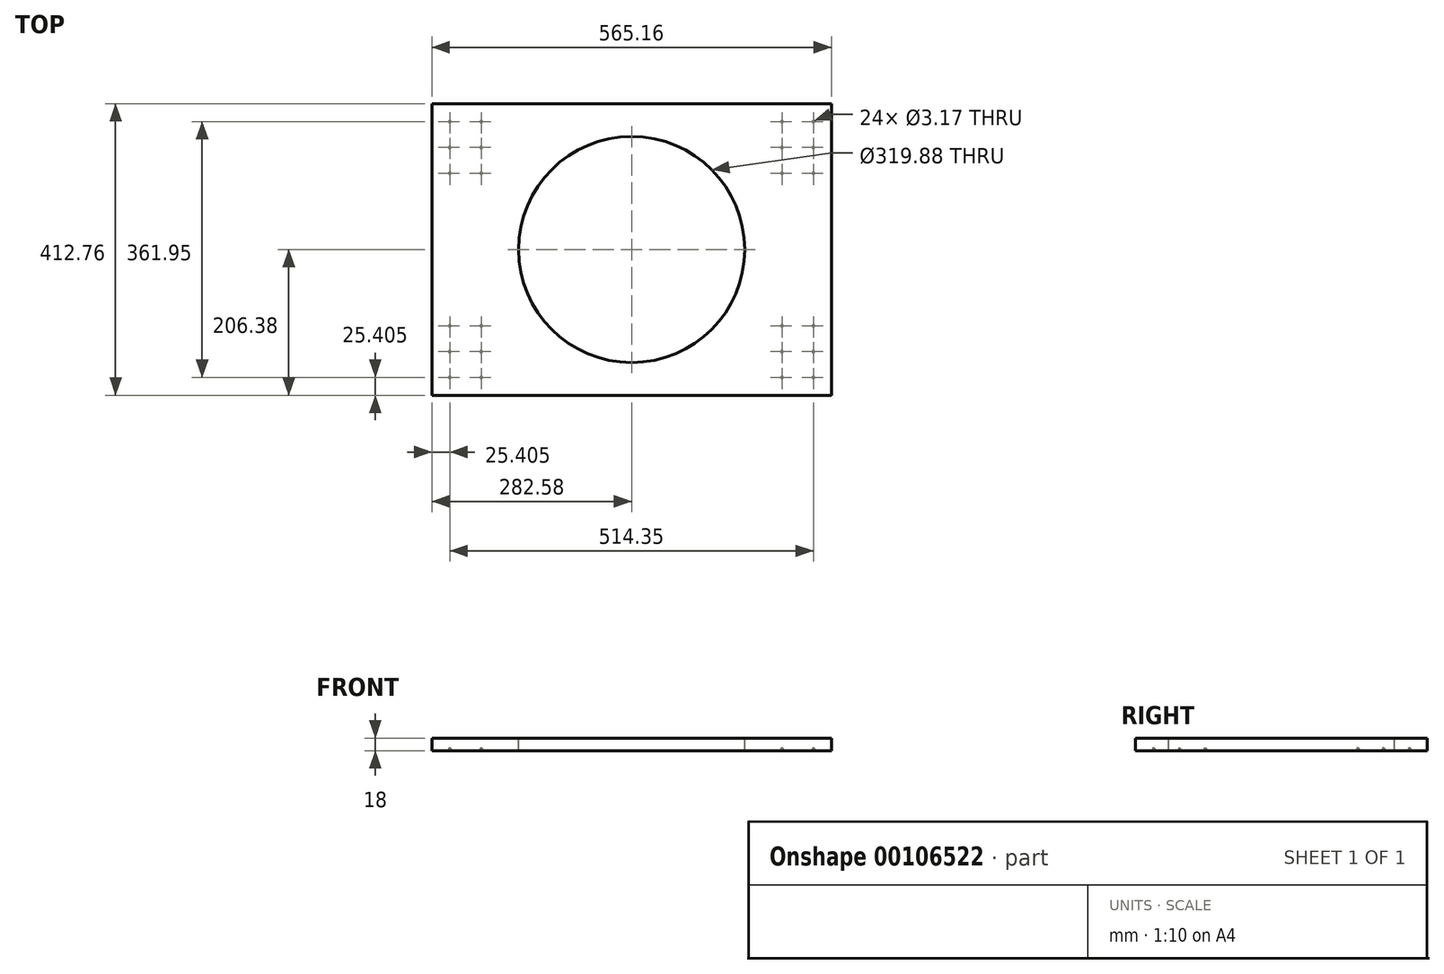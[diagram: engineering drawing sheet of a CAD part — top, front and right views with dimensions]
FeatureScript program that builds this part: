
annotation { "Feature Type Name" : "Feature", "Feature Type Description" : "" }
export const myFeature = defineFeature(function(context is Context, id is Id, definition is map)
    precondition{}
    {
        {
            var Q0;
            Q0=qCreatedBy(makeId("Top.planeOp"),FACE);
            var sketch = newSketch(context, id + "F0", { "sketchPlane" : qUnion([Q0])});
            skLineSegment(sketch, "E0.bottom", {"start": v(282.58, -206.38) * mm, "end": v(-282.57, -206.38) * mm});
            skLineSegment(sketch, "E0.top", {"start": v(282.57, 206.38) * mm, "end": v(-282.57, 206.38) * mm});
            skLineSegment(sketch, "E0.left", {"start": v(282.57, -206.38) * mm, "end": v(282.57, 206.38) * mm});
            skLineSegment(sketch, "E0.right", {"start": v(-282.57, -206.38) * mm, "end": v(-282.57, 206.37) * mm});
            skPoint(sketch, "E0.middle", {"position": v(0, 0) * mm});
            skSolve(sketch);
        }
        {
            var Q0;
            Q0=makeQuery(id+"F0.imprint","IMPRINT",FACE,{"disambiguationData":[TD([[makeQuery(id+"F0.imprint","IMPRINT",EDGE,{"derivedFrom":sQuery(id+"F0.wireOp",EDGE,"E0.bottom")}),-1.0]])]});
            extrude(context, id + "F1", {"entities" : qUnion([Q0]), "depth" : 18 * mm});
        }
        {
            var Q0;
            Q0=makeQuery(id+"F1.opExtrude","CAP_FACE",FACE,{"disambiguationData":[OSD([sQuery(id+"F0.wireOp",EDGE,"E0.bottom"),sQuery(id+"F0.wireOp",EDGE,"E0.top"),sQuery(id+"F0.wireOp",EDGE,"E0.left"),sQuery(id+"F0.wireOp",EDGE,"E0.right")])],"isStart":false});
            var sketch = newSketch(context, id + "F2", { "sketchPlane" : qUnion([Q0])});
            skCircle(sketch, "E1", {"center": v(0, 0) * mm, "radius": 159.94 * mm});
            skSolve(sketch);
        }
        {
            var Q0;
            Q0=makeQuery(id+"F2.imprint","IMPRINT",FACE,{"disambiguationData":[TD([[makeQuery(id+"F2.imprint","IMPRINT",EDGE,{"derivedFrom":sQuery(id+"F2.wireOp",EDGE,"E1")}),1.0]])]});
            extrude(context, id + "F3", {"entities" : qUnion([Q0]), "operationType" : NewBodyOperationType.REMOVE, "endBound" : BoundingType.THROUGH_ALL, "oppositeDirection" : true, "depth" : 25.4 * mm});
        }
        {
            var Q0;
            Q0=makeQuery(id+"F1.opExtrude","CAP_FACE",FACE,{"disambiguationData":[OSD([sQuery(id+"F0.wireOp",EDGE,"E0.bottom"),sQuery(id+"F0.wireOp",EDGE,"E0.top"),sQuery(id+"F0.wireOp",EDGE,"E0.left"),sQuery(id+"F0.wireOp",EDGE,"E0.right")])],"isStart":true});
            var sketch = newSketch(context, id + "F4", { "sketchPlane" : qUnion([Q0])});
            skPoint(sketch, "E2", {"position": v(-257.18, -180.97) * mm});
            skPoint(sketch, "E3", {"position": v(-257.18, -144.46) * mm});
            skPoint(sketch, "E4", {"position": v(-257.18, -107.95) * mm});
            skPoint(sketch, "E5", {"position": v(-212.72, -107.95) * mm});
            skPoint(sketch, "E6", {"position": v(-212.72, -144.46) * mm});
            skPoint(sketch, "E7", {"position": v(-212.72, -180.97) * mm});
            skLineSegment(sketch, "E8", {"start": v(0, -206.38) * mm, "end": v(0, 206.38) * mm, "construction": true});
            skLineSegment(sketch, "E9", {"start": v(-282.57, 0) * mm, "end": v(282.57, 0) * mm, "construction": true});
            skPoint(sketch, "E10.MirrorP", {"position": v(212.72, -180.98) * mm});
            skPoint(sketch, "E11.MirrorP", {"position": v(257.17, -180.98) * mm});
            skPoint(sketch, "E12.MirrorP", {"position": v(257.18, -144.46) * mm});
            skPoint(sketch, "E13.MirrorP", {"position": v(212.72, -144.46) * mm});
            skPoint(sketch, "E14.MirrorP", {"position": v(212.72, -107.95) * mm});
            skPoint(sketch, "E15.MirrorP", {"position": v(257.18, -107.95) * mm});
            skPoint(sketch, "E16.MirrorP", {"position": v(-212.72, 107.95) * mm});
            skPoint(sketch, "E17.MirrorP", {"position": v(-257.17, 107.95) * mm});
            skPoint(sketch, "E18.MirrorP", {"position": v(-257.17, 144.46) * mm});
            skPoint(sketch, "E19.MirrorP", {"position": v(-212.72, 144.46) * mm});
            skPoint(sketch, "E20.MirrorP", {"position": v(-212.72, 180.98) * mm});
            skPoint(sketch, "E21.MirrorP", {"position": v(-257.17, 180.98) * mm});
            skPoint(sketch, "E22.MirrorP", {"position": v(212.72, 180.98) * mm});
            skPoint(sketch, "E23.MirrorP", {"position": v(257.18, 144.46) * mm});
            skPoint(sketch, "E24.MirrorP", {"position": v(212.72, 144.46) * mm});
            skPoint(sketch, "E25.MirrorP", {"position": v(212.72, 107.95) * mm});
            skPoint(sketch, "E26.MirrorP", {"position": v(257.18, 107.95) * mm});
            skPoint(sketch, "E27.MirrorP", {"position": v(257.18, 180.97) * mm});
            skSolve(sketch);
        }
        {
            var Q0;
            Q0=sQuery(id+"F4.wireOp",VERTEX,"E2");
            var Q1;
            Q1=sQuery(id+"F4.wireOp",VERTEX,"E7");
            var Q2;
            Q2=sQuery(id+"F4.wireOp",VERTEX,"E6");
            var Q3;
            Q3=sQuery(id+"F4.wireOp",VERTEX,"E3");
            var Q4;
            Q4=sQuery(id+"F4.wireOp",VERTEX,"E4");
            var Q5;
            Q5=sQuery(id+"F4.wireOp",VERTEX,"E5");
            var Q6;
            Q6=sQuery(id+"F4.wireOp",VERTEX,"E17.MirrorP");
            var Q7;
            Q7=sQuery(id+"F4.wireOp",VERTEX,"E16.MirrorP");
            var Q8;
            Q8=sQuery(id+"F4.wireOp",VERTEX,"E18.MirrorP");
            var Q9;
            Q9=sQuery(id+"F4.wireOp",VERTEX,"E19.MirrorP");
            var Q10;
            Q10=sQuery(id+"F4.wireOp",VERTEX,"E21.MirrorP");
            var Q11;
            Q11=sQuery(id+"F4.wireOp",VERTEX,"E20.MirrorP");
            var Q12;
            Q12=sQuery(id+"F4.wireOp",VERTEX,"E22.MirrorP");
            var Q13;
            Q13=sQuery(id+"F4.wireOp",VERTEX,"E27.MirrorP");
            var Q14;
            Q14=sQuery(id+"F4.wireOp",VERTEX,"E23.MirrorP");
            var Q15;
            Q15=sQuery(id+"F4.wireOp",VERTEX,"E24.MirrorP");
            var Q16;
            Q16=sQuery(id+"F4.wireOp",VERTEX,"E25.MirrorP");
            var Q17;
            Q17=sQuery(id+"F4.wireOp",VERTEX,"E26.MirrorP");
            var Q18;
            Q18=sQuery(id+"F4.wireOp",VERTEX,"E14.MirrorP");
            var Q19;
            Q19=sQuery(id+"F4.wireOp",VERTEX,"E15.MirrorP");
            var Q20;
            Q20=sQuery(id+"F4.wireOp",VERTEX,"E13.MirrorP");
            var Q21;
            Q21=sQuery(id+"F4.wireOp",VERTEX,"E11.MirrorP");
            var Q22;
            Q22=sQuery(id+"F4.wireOp",VERTEX,"E12.MirrorP");
            var Q23;
            Q23=sQuery(id+"F4.wireOp",VERTEX,"E10.MirrorP");
            var Q24;
            Q24=makeQuery(id+"F1.opExtrude","SWEPT_BODY",BODY,{"disambiguationData":[OSD([sQuery(id+"F0.wireOp",EDGE,"E0.bottom"),sQuery(id+"F0.wireOp",EDGE,"E0.top"),sQuery(id+"F0.wireOp",EDGE,"E0.left"),sQuery(id+"F0.wireOp",EDGE,"E0.right")])]});
            hole(context, id + "F5", {"style" : HoleStyle.SIMPLE, "endStyle" : HoleEndStyle.BLIND, "holeDiameter" : 3.17 * mm, "holeDepth" : 3.17 * mm, "startFromSketch" : true, "locations" : qUnion([Q0, Q1, Q2, Q3, Q4, Q5, Q6, Q7, Q8, Q9, Q10, Q11, Q12, Q13, Q14, Q15, Q16, Q17, Q18, Q19, Q20, Q21, Q22, Q23]), "scope" : qUnion([Q24])});
        }
    });
